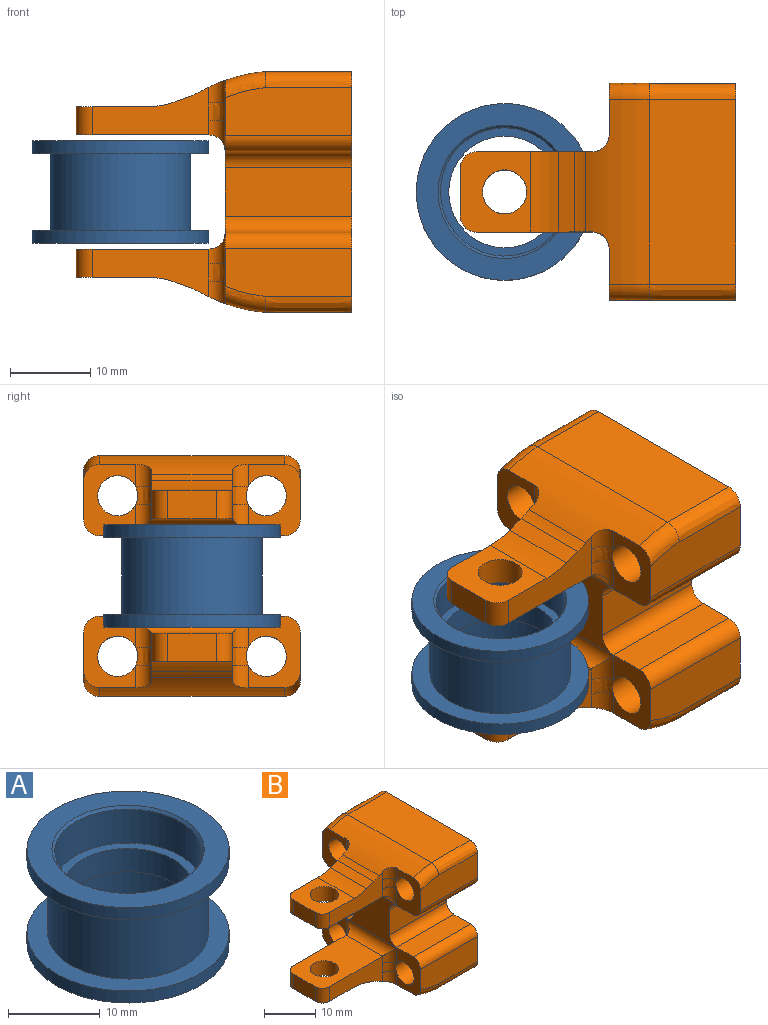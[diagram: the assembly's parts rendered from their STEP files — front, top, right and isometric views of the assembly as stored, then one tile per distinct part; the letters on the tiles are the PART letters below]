
ASSEMBLY  parts=2 mates=1
PART A: 14 faces, bbox 22x22x12.7 mm
  f0: cylinder r=6.94mm len=13.89mm, axis (0,0,1), area 135.3mm2, adj f1,f11
  f1: plane 15.97x15.97mm, normal (0,0,1), area 48.9mm2, adj f0,f2
  f2: cylinder r=7.99mm len=15.97mm, axis (0,0,1), area 225.8mm2, adj f1,f13
  f3: plane 22x22mm, normal (0,0,1), area 164.4mm2, adj f4,f13
  f4: cylinder r=11mm len=22mm, axis (0,0,1), area 110.6mm2, adj f3,f5
  f5: plane 22x22mm, normal (0,0,-1), area 139.6mm2, adj f4,f6
  f6: cylinder r=8.75mm len=17.5mm, axis (0,0,1), area 522.3mm2, adj f5,f7
  f7: plane 22x22mm, normal (0,0,1), area 139.6mm2, adj f6,f8
  f8: cylinder r=11mm len=22mm, axis (0,0,1), area 110.6mm2, adj f7,f9
  f9: plane 22x22mm, normal (0,0,-1), area 164.4mm2, adj f8,f12
  f10: cylinder r=7.99mm len=15.97mm, axis (0,0,1), area 225.8mm2, adj f11,f12
  f11: plane 15.97x15.97mm, normal (0,0,-1), area 48.9mm2, adj f0,f10
  f12: cone r=8.29mm half-angle=45deg, axis (0,0,-1), area 21.7mm2, adj f9,f10
  f13: cone r=7.99mm half-angle=45deg, axis (0,0,1), area 21.7mm2, adj f2,f3
PART B: 72 faces, bbox 34.6x27.4x30.8 mm
  f0: plane 14.52x5.95mm, normal (0,-1,0), area 57.7mm2, adj f6,f8,f25,f30,f31,f34,f43,f44
  f1: plane 15.75x6mm, normal (0,-1,0), area 94.5mm2, adj f9,f54,f59,f71
  f2: plane 14.52x5.95mm, normal (0,1,0), area 57.7mm2, adj f6,f8,f25,f30,f31,f34,f39,f40
  f3: plane 15.75x6mm, normal (0,1,0), area 94.5mm2, adj f9,f56,f58,f71
  f4: plane 14.52x5.95mm, normal (0,1,0), area 57.7mm2, adj f10,f12,f26,f29,f32,f33,f46,f47
  f5: plane 14.52x5.95mm, normal (0,-1,0), area 57.7mm2, adj f10,f12,f26,f29,f32,f33,f49,f51
  f6: plane 16.5x10mm, normal (0,0,1), area 139.5mm2, adj f0,f2,f7,f28,f42,f62,f64
  f7: plane 6x3.5mm, normal (-1,0,0), area 21mm2, adj f6,f8,f62,f64
  f8: plane 10x8.74mm, normal (0,0,-1), area 61.9mm2, adj f0,f2,f7,f28,f30,f62,f64
  f9: plane 28.15x27.35mm, normal (-1,0,0), area 253.4mm2, adj f1,f3,f13,f14,f15,f16,f17,f18
  f10: plane 10x8.74mm, normal (0,0,1), area 61.9mm2, adj f4,f5,f11,f27,f29,f61,f63
  f11: plane 6x3.5mm, normal (-1,0,0), area 21mm2, adj f10,f12,f61,f63
  f12: plane 16.5x10mm, normal (0,0,-1), area 139.5mm2, adj f4,f5,f11,f27,f50,f61,f63
  f13: plane 15.75x5.99mm, normal (0,-1,0), area 91.9mm2, adj f9,f37,f60,f70,f71
  f14: plane 15.75x4.5mm, normal (0,0,-1), area 70.9mm2, adj f9,f59,f60,f71
  f15: cylinder r=2.5mm len=15.75mm, axis (1,0,0), area 247.4mm2, adj f9,f51,f71
  f16: plane 15.75x5.99mm, normal (0,1,0), area 91.9mm2, adj f9,f38,f57,f68,f71
  f17: cylinder r=2.5mm len=15.75mm, axis (1,0,0), area 247.4mm2, adj f9,f47,f71
  f18: plane 15.75x4.5mm, normal (0,0,-1), area 70.9mm2, adj f9,f57,f58,f71
  f19: plane 15.75x4.5mm, normal (0,0,1), area 70.9mm2, adj f9,f55,f56,f71
  f20: plane 15.75x5.99mm, normal (0,1,0), area 91.9mm2, adj f9,f36,f55,f67,f71
  f21: cylinder r=2.5mm len=15.75mm, axis (1,0,0), area 247.4mm2, adj f9,f40,f71
  f22: plane 15.75x5.99mm, normal (0,-1,0), area 91.9mm2, adj f9,f35,f53,f65,f71
  f23: cylinder r=2.5mm len=15.75mm, axis (1,0,0), area 247.4mm2, adj f9,f44,f71
  f24: plane 15.75x4.5mm, normal (0,0,1), area 70.9mm2, adj f9,f53,f54,f71
  f25: plane 10x2.03mm, normal (-0.34,0,-0.94), area 21.6mm2, adj f0,f2,f30,f31
  f26: plane 10x2.03mm, normal (-0.34,0,0.94), area 21.6mm2, adj f4,f5,f29,f32
  f27: cylinder r=2.75mm len=5.5mm, axis (0,0,1), area 60.5mm2, adj f10,f12
  f28: cylinder r=2.75mm len=5.5mm, axis (0,0,1), area 60.5mm2, adj f6,f8
  f29: cylinder r=10mm len=10mm, axis (0,-1,0), area 34.9mm2, adj f4,f5,f10,f26
  f30: cylinder r=10mm len=10mm, axis (0,1,0), area 34.9mm2, adj f0,f2,f8,f25
  f31: cylinder r=10mm len=10mm, axis (0,1,0), area 15.6mm2, adj f0,f2,f25,f34
  f32: cylinder r=10mm len=10mm, axis (0,1,0), area 15.6mm2, adj f4,f5,f26,f33
  f33: cylinder r=20mm len=23mm, axis (0,1,0), area 151.8mm2, adj f4,f5,f9,f32,f37,f38,f46,f49
  f34: cylinder r=20mm len=23mm, axis (0,1,0), area 151.8mm2, adj f0,f2,f9,f31,f35,f36,f39,f45
  f35: torus R=18mm, axis (0,1,0), area 16.4mm2, adj f9,f22,f34,f65
  f36: torus R=18mm, axis (0,1,0), area 16.4mm2, adj f9,f20,f34,f67
  f37: torus R=18mm, axis (0,-1,0), area 16.4mm2, adj f9,f13,f33,f70
  f38: torus R=18mm, axis (0,-1,0), area 16.4mm2, adj f9,f16,f33,f68
  f39: cylinder r=2mm len=2.81mm, axis (0,0,1), area 7.5mm2, adj f2,f9,f34,f40
  f40: bspline ~2.96x2.18mm, area 6.5mm2, adj f2,f21,f39,f41
  f41: cylinder r=2mm len=3.81mm, axis (0,0,1), area 8.8mm2, adj f2,f9,f40,f42
  f42: cylinder r=2mm len=14mm, axis (0,1,0), area 37.7mm2, adj f6,f9,f41,f43
  f43: cylinder r=2mm len=3.81mm, axis (0,0,-1), area 8.8mm2, adj f0,f9,f42,f44
  f44: bspline ~2.96x2.18mm, area 6.5mm2, adj f0,f23,f43,f45
  f45: cylinder r=2mm len=2.81mm, axis (0,0,-1), area 7.5mm2, adj f0,f9,f34,f44
  f46: cylinder r=2mm len=2.81mm, axis (0,0,1), area 7.5mm2, adj f4,f9,f33,f47
  f47: bspline ~2.96x2.18mm, area 6.5mm2, adj f4,f17,f46,f48
  f48: cylinder r=2mm len=3.81mm, axis (0,0,1), area 8.8mm2, adj f4,f9,f47,f50
  f49: cylinder r=2mm len=2.81mm, axis (0,0,-1), area 7.5mm2, adj f5,f9,f33,f51
  f50: cylinder r=2mm len=14mm, axis (0,-1,0), area 37.7mm2, adj f9,f12,f48,f52
  f51: bspline ~2.96x2.18mm, area 6.5mm2, adj f5,f15,f49,f52
  f52: cylinder r=2mm len=3.81mm, axis (0,0,-1), area 8.8mm2, adj f5,f9,f50,f51
  f53: cylinder r=2mm len=15.75mm, axis (1,0,0), area 49.5mm2, adj f9,f22,f24,f71
  f54: cylinder r=2mm len=15.75mm, axis (1,0,0), area 49.5mm2, adj f1,f9,f24,f71
  f55: cylinder r=2mm len=15.75mm, axis (1,0,0), area 49.5mm2, adj f9,f19,f20,f71
  f56: cylinder r=2mm len=15.75mm, axis (1,0,0), area 49.5mm2, adj f3,f9,f19,f71
  f57: cylinder r=2mm len=15.75mm, axis (1,0,0), area 49.5mm2, adj f9,f16,f18,f71
  f58: cylinder r=2mm len=15.75mm, axis (-1,0,0), area 49.5mm2, adj f3,f9,f18,f71
  f59: cylinder r=2mm len=15.75mm, axis (-1,0,0), area 49.5mm2, adj f1,f9,f14,f71
  f60: cylinder r=2mm len=15.75mm, axis (1,0,0), area 49.5mm2, adj f9,f13,f14,f71
  f61: cylinder r=2mm len=3.5mm, axis (0,0,-1), area 11mm2, adj f4,f10,f11,f12
  f62: cylinder r=2mm len=3.5mm, axis (0,0,-1), area 11mm2, adj f2,f6,f7,f8
  f63: cylinder r=2mm len=3.5mm, axis (0,0,1), area 11mm2, adj f5,f10,f11,f12
  f64: cylinder r=2mm len=3.5mm, axis (0,0,1), area 11mm2, adj f0,f6,f7,f8
  f65: extruded ~10.75x2.01mm, area 33.9mm2, adj f22,f35,f66,f71
  f66: plane 23x10.75mm, normal (0,0,-1), area 247.3mm2, adj f34,f65,f67,f71
  f67: extruded ~10.75x2.01mm, area 33.8mm2, adj f20,f36,f66,f71
  f68: extruded ~10.75x2.01mm, area 33.9mm2, adj f16,f38,f69,f71
  f69: plane 23x10.75mm, normal (0,0,1), area 247.3mm2, adj f33,f68,f70,f71
  f70: extruded ~10.75x2.01mm, area 33.8mm2, adj f13,f37,f69,f71
  f71: plane 30x27mm, normal (1,0,0), area 558mm2, adj f1,f3,f13,f14,f15,f16,f17,f18
PLACE A t=(-7,1.71,0.94)mm
PLACE B t=(-7,1.71,0.94)mm fixed
MATE revolute A.f0 <-> B.f27  axis (0,0,1) through (-7,1.71,7.29)mm
